# Revit family: Shower-Shower_Column_Kit-KOHLER-ALEO-K-97822T_
name_source: partatom
category: Plumbing Fixtures
units: mm (PartAtom-declared; Revit-internal decimal feet)

## family parameters
Cut with Voids When Loaded = No
Host = Face
OmniClass Number = 23.31.17.00
OmniClass Title = Showers
Part Type = Normal
Room Calculation Point = No
Round Connector Dimension = Use Diameter
Shared = No

## types (4) — shared parameters
ADA Compliant = No
Assembly Code = D2010700
CW Connection = Yes
Cold Water Inlet = Cold Water Inlet
Date Modified = 11/06/2023
Default Elevation = 42"
Drain Included = No
Flow Rate = 3 GPM
HW Connection = Yes
Height = 48 11/16"
Hot Water Inlet = Hot Water Inlet
Length = 24 1/4"
Manufacturer = Kohler Co.
Master Format 2014 = 22 42 23
Master Format 2014 Name = Residential Showers
Material = Premium Metal Construction
Pressure = 80.00 psi
Product Documentation Link = https://files.kohler.com.cn
Product Name = ALEO
URL = https://www.kohler.com.cn
Vent Connection = No
Waste Connection = No
Waste Water Outlet = Waste Water Outlet
WaterSense Certified = No
Width = 12 3/8"

## per-type parameters (varying)
| type | 9 | B9 | Description | Finish | Model | Nozzle Finish | Product Page URL | Secondary Finish | Type |
| 9, CP-Polished Chrome | Yes | No | Thermostatic double rain shower column hard pipe connection | Kohler-Metal-CP-Polished_Chrome | K-97822T-9-CP | Kohler-Plastic-0-White | https://www.kohler.com.cn | Kohler-Plastic-0-White | 1 |
| 9E, CP-Polished Chrome | Yes | No | Thermostatic Dual Shower Column | Kohler-Metal-CP-Polished_Chrome | K-97822T-9E-CP | Kohler-Plastic-0-White |  | Kohler-Plastic-0-White | 2 |
| 9, BL-Matte Black | Yes | No | Thermostatic double rain shower column hard pipe connection | Kohler-Metal-BL-Matte_Black | K-97822T-9-BL | Plastic-Pantone-412C |  | Silicone-Pantone-PQ-194205-TCX | 3 |
| B9, CP-Polished Chrome | No | Yes | Thermostat Double Rain Shower Column – Rigid Pipe Connection | Kohler-Metal-CP-Polished_Chrome | K-97822T-B9-CP | Kohler-Plastic-0-White | https://www.kohler.com.cn | Kohler-Plastic-0-White | 4 |

## geometry (parser evidence)
native form markers: Sweep x7
no freeform markers — native parametric forms only
